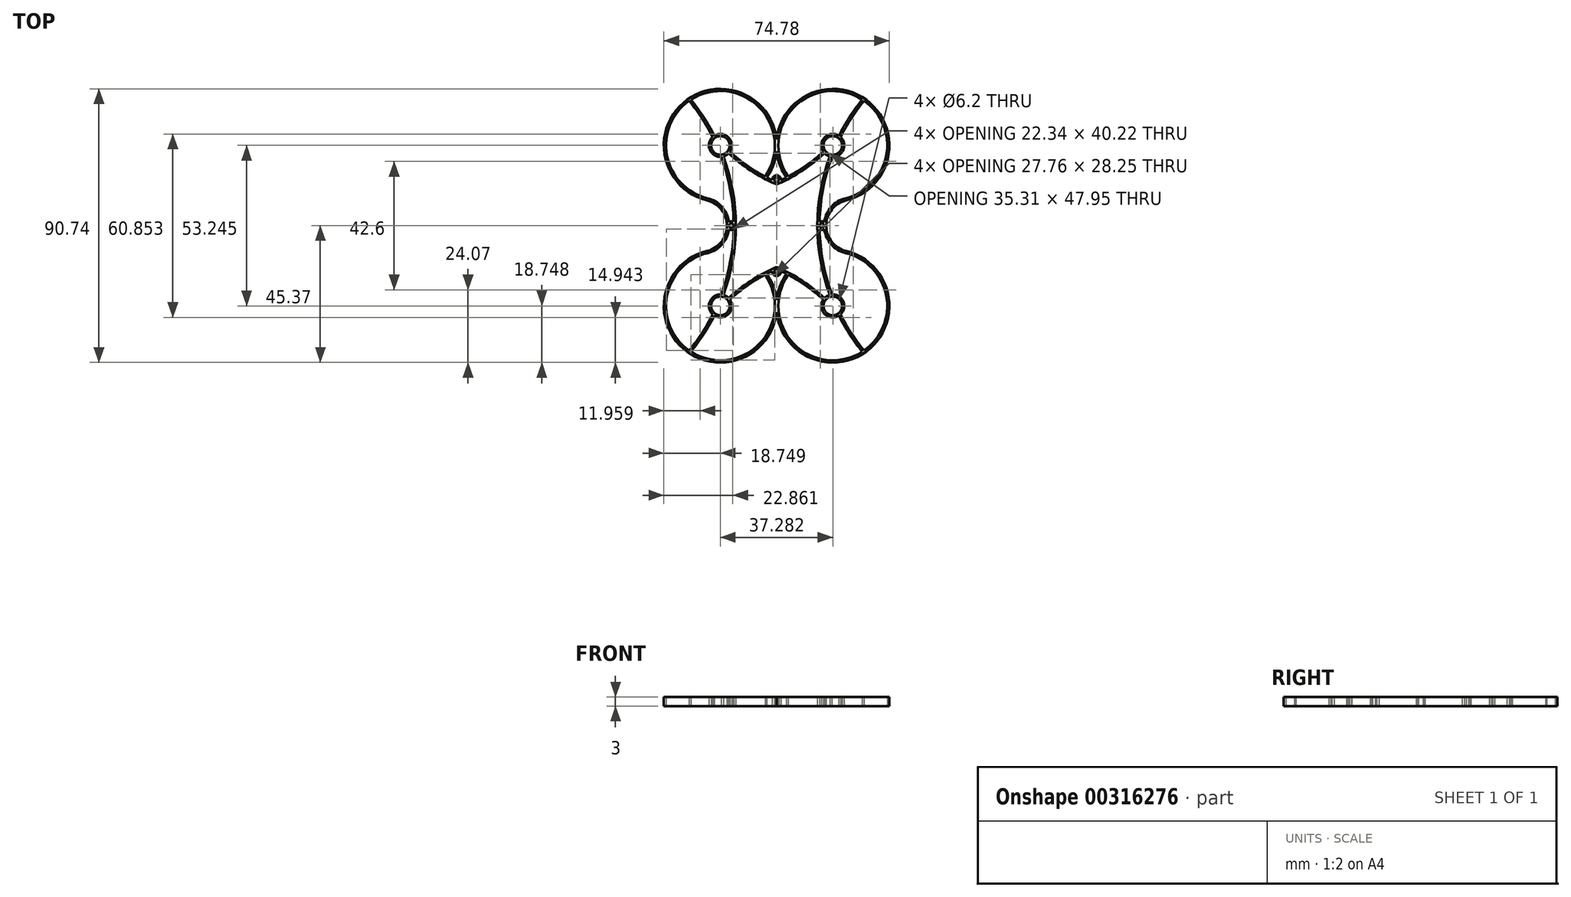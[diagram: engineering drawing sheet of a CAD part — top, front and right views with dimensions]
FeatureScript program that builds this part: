
annotation { "Feature Type Name" : "Feature", "Feature Type Description" : "" }
export const myFeature = defineFeature(function(context is Context, id is Id, definition is map)
    precondition{}
    {
        {
            var Q0;
            Q0=qCreatedBy(makeId("Top.planeOp"),FACE);
            var sketch = newSketch(context, id + "F0", { "sketchPlane" : qUnion([Q0])});
            skCircle(sketch, "E0", {"center": v(0, 0) * mm, "radius": 32.5 * mm, "construction": true});
            skLineSegment(sketch, "E1", {"start": v(0, 0) * mm, "end": v(37.3, 53.28) * mm, "construction": true});
            skPoint(sketch, "E2", {"position": v(18.64, 26.62) * mm});
            skCircle(sketch, "E3", {"center": v(18.64, 26.62) * mm, "radius": 15 * mm, "construction": true});
            skCircle(sketch, "E4", {"center": v(0, 0) * mm, "radius": 15 * mm, "construction": true});
            skPoint(sketch, "E5", {"position": v(15, 0) * mm});
            skPoint(sketch, "E6", {"position": v(0, 15.25) * mm});
            skCircle(sketch, "E7", {"center": v(0, 15.25) * mm, "radius": 0.75 * mm});
            skCircle(sketch, "E8.0", {"center": v(0, 15.25) * mm, "radius": 1.45 * mm});
            skCircle(sketch, "E9", {"center": v(15, 0) * mm, "radius": 0.75 * mm});
            skCircle(sketch, "E10.0", {"center": v(15, 0) * mm, "radius": 1.45 * mm});
            skLineSegment(sketch, "E11", {"start": v(0, 0) * mm, "end": v(0, 39.87) * mm, "construction": true});
            skCircle(sketch, "E12", {"center": v(18.64, 26.62) * mm, "radius": 18.75 * mm});
            skCircle(sketch, "E13.0", {"center": v(18.64, 26.62) * mm, "radius": 18.05 * mm});
            skArc(sketch, "E14", {"start": v(22.93, 9.09) * mm, "mid": v(17.76, 5.8) * mm, "end": v(15.75, 0) * mm});
            skArc(sketch, "E15.0", {"start": v(23.1, 8.4) * mm, "mid": v(18.31, 5.36) * mm, "end": v(16.45, 0) * mm});
            skCircle(sketch, "E16", {"center": v(18.64, 26.62) * mm, "radius": 3.1 * mm});
            skCircle(sketch, "E17.0", {"center": v(18.64, 26.62) * mm, "radius": 3.8 * mm});
            skArc(sketch, "E18", {"start": v(29, 41.4) * mm, "mid": v(28.04, 40.21) * mm, "end": v(27.12, 39) * mm});
            skArc(sketch, "E19.0", {"start": v(28.86, 42.34) * mm, "mid": v(24.21, 36.03) * mm, "end": v(20.34, 29.21) * mm});
            skArc(sketch, "E20", {"start": v(0.6, 13.93) * mm, "mid": v(8.65, 18.35) * mm, "end": v(15.91, 23.98) * mm});
            skArc(sketch, "E21.0", {"start": v(0.22, 14.53) * mm, "mid": v(8.25, 18.92) * mm, "end": v(15.47, 24.52) * mm});
            skArc(sketch, "E22.trimOffspring", {"start": v(18.64, 26.62) * mm, "mid": v(18.64, 26.63) * mm, "end": v(18.65, 26.63) * mm});
            skArc(sketch, "E23.trimOffspring", {"start": v(18.36, 22.83) * mm, "mid": v(15.29, 11.6) * mm, "end": v(14.25, 0) * mm});
            skArc(sketch, "E24.trimOffspring", {"start": v(17.66, 22.95) * mm, "mid": v(14.58, 11.66) * mm, "end": v(13.55, 0) * mm});
            skArc(sketch, "E25.trimOffspring", {"start": v(27.12, 39) * mm, "mid": v(23.77, 34.02) * mm, "end": v(20.9, 28.75) * mm});
            skSolve(sketch);
        }
        {
            var Q0;
            Q0=makeQuery(id+"F0.imprint","IMPRINT",FACE,{"disambiguationData":[TD([[makeQuery(id+"F0.imprint","IMPRINT",EDGE,{"derivedFrom":sQuery(id+"F0.wireOp",EDGE,"E7")}),-1.0]])]});
            var Q1;
            {var subQ0=sQuery(id+"F0.wireOp",EDGE,"E20");var subQ1=sQuery(id+"F0.wireOp",EDGE,"E8.0");var subQ2=makeQuery(id+"F0.imprint","INTERSECT",VERTEX,{"derivedFrom":[subQ1,subQ0]});Q1=makeQuery(id+"F0.imprint","IMPRINT",FACE,{"disambiguationData":[TD([[makeQuery(id+"F0.imprint","IMPRINT",EDGE,{"disambiguationData":[TD([[subQ2,-1.0]])],"derivedFrom":subQ1}),-1.0]])]});}
            var Q2;
            {var subQ0=sQuery(id+"F0.wireOp",EDGE,"E15.0");var subQ1=sQuery(id+"F0.wireOp",EDGE,"E10.0");var subQ2=makeQuery(id+"F0.imprint","INTERSECT",VERTEX,{"derivedFrom":[subQ1,subQ0]});Q2=makeQuery(id+"F0.imprint","IMPRINT",FACE,{"disambiguationData":[TD([[makeQuery(id+"F0.imprint","IMPRINT",EDGE,{"disambiguationData":[TD([[subQ2,-1.0]])],"derivedFrom":subQ1}),-1.0]])]});}
            var Q3;
            {var subQ0=sQuery(id+"F0.wireOp",EDGE,"E24.trimOffspring");var subQ1=sQuery(id+"F0.wireOp",EDGE,"E10.0");var subQ2=makeQuery(id+"F0.imprint","INTERSECT",VERTEX,{"derivedFrom":[subQ1,subQ0]});Q3=makeQuery(id+"F0.imprint","IMPRINT",FACE,{"disambiguationData":[TD([[makeQuery(id+"F0.imprint","IMPRINT",EDGE,{"disambiguationData":[TD([[subQ2,1.0]])],"derivedFrom":subQ1}),-1.0]])]});}
            var Q4;
            {var subQ0=sQuery(id+"F0.wireOp",EDGE,"E19.0");var subQ1=sQuery(id+"F0.wireOp",EDGE,"E12");var subQ2=makeQuery(id+"F0.imprint","INTERSECT",VERTEX,{"derivedFrom":[subQ1,subQ0]});Q4=makeQuery(id+"F0.imprint","IMPRINT",FACE,{"disambiguationData":[TD([[makeQuery(id+"F0.imprint","IMPRINT",EDGE,{"disambiguationData":[TD([[subQ2,-1.0]])],"derivedFrom":subQ1}),1.0]])]});}
            var Q5;
            {var subQ5=sQuery(id+"F0.wireOp",EDGE,"E14");var subQ7=sQuery(id+"F0.wireOp",EDGE,"E9");var subQ8=makeQuery(id+"F0.imprint","INTERSECT",VERTEX,{"derivedFrom":[subQ7,subQ5]});Q5=makeQuery(id+"F0.imprint","IMPRINT",FACE,{"disambiguationData":[TD([[makeQuery(id+"F0.imprint","IMPRINT",EDGE,{"disambiguationData":[TD([[subQ8,1.0]])],"derivedFrom":subQ7}),-1.0]])]});}
            var Q6;
            {var subQ0=sQuery(id+"F0.wireOp",EDGE,"E21.0");var subQ1=sQuery(id+"F0.wireOp",EDGE,"E12");var subQ2=makeQuery(id+"F0.imprint","INTERSECT",VERTEX,{"derivedFrom":[subQ1,subQ0]});Q6=makeQuery(id+"F0.imprint","IMPRINT",FACE,{"disambiguationData":[TD([[makeQuery(id+"F0.imprint","IMPRINT",EDGE,{"disambiguationData":[TD([[subQ2,-1.0]])],"derivedFrom":subQ1}),1.0]])]});}
            var Q7;
            {var subQ0=sQuery(id+"F0.wireOp",EDGE,"E24.trimOffspring");var subQ1=sQuery(id+"F0.wireOp",EDGE,"E12");var subQ2=makeQuery(id+"F0.imprint","INTERSECT",VERTEX,{"derivedFrom":[subQ1,subQ0]});Q7=makeQuery(id+"F0.imprint","IMPRINT",FACE,{"disambiguationData":[TD([[makeQuery(id+"F0.imprint","IMPRINT",EDGE,{"disambiguationData":[TD([[subQ2,-1.0]])],"derivedFrom":subQ1}),1.0]])]});}
            var Q8;
            {var subQ6=sQuery(id+"F0.wireOp",EDGE,"E12");var subQ8=makeQuery(id+"F0.imprint","INTERSECT",VERTEX,{"derivedFrom":[subQ6,sQuery(id+"F0.wireOp",EDGE,"E15.0")]});Q8=makeQuery(id+"F0.imprint","IMPRINT",FACE,{"disambiguationData":[TD([[makeQuery(id+"F0.imprint","IMPRINT",EDGE,{"disambiguationData":[TD([[subQ8,1.0]])],"derivedFrom":subQ6}),1.0]])]});}
            var Q9;
            {var subQ0=sQuery(id+"F0.wireOp",EDGE,"E14");var subQ1=sQuery(id+"F0.wireOp",EDGE,"E9");var subQ2=makeQuery(id+"F0.imprint","INTERSECT",VERTEX,{"derivedFrom":[subQ1,subQ0]});Q9=makeQuery(id+"F0.imprint","IMPRINT",FACE,{"disambiguationData":[TD([[makeQuery(id+"F0.imprint","IMPRINT",EDGE,{"disambiguationData":[TD([[subQ2,-1.0]])],"derivedFrom":subQ1}),-1.0]])]});}
            var Q10;
            {var subQ0=sQuery(id+"F0.wireOp",EDGE,"E24.trimOffspring");var subQ1=sQuery(id+"F0.wireOp",EDGE,"E13.0");var subQ2=makeQuery(id+"F0.imprint","INTERSECT",VERTEX,{"derivedFrom":[subQ1,subQ0]});Q10=makeQuery(id+"F0.imprint","IMPRINT",FACE,{"disambiguationData":[TD([[makeQuery(id+"F0.imprint","IMPRINT",EDGE,{"disambiguationData":[TD([[subQ2,-1.0]])],"derivedFrom":subQ1}),1.0]])]});}
            var Q11;
            {var subQ0=sQuery(id+"F0.wireOp",EDGE,"E21.0");var subQ1=sQuery(id+"F0.wireOp",EDGE,"E13.0");var subQ2=makeQuery(id+"F0.imprint","INTERSECT",VERTEX,{"derivedFrom":[subQ1,subQ0]});Q11=makeQuery(id+"F0.imprint","IMPRINT",FACE,{"disambiguationData":[TD([[makeQuery(id+"F0.imprint","IMPRINT",EDGE,{"disambiguationData":[TD([[subQ2,-1.0]])],"derivedFrom":subQ1}),1.0]])]});}
            var Q12;
            {var subQ5=sQuery(id+"F0.wireOp",EDGE,"E16");var subQ8=sQuery(id+"F0.wireOp",EDGE,"E19.0");var subQ10=makeQuery(id+"F0.imprint","INTERSECT",VERTEX,{"derivedFrom":[subQ5,subQ8]});Q12=makeQuery(id+"F0.imprint","IMPRINT",FACE,{"disambiguationData":[TD([[makeQuery(id+"F0.imprint","IMPRINT",EDGE,{"disambiguationData":[TD([[subQ10,-1.0]])],"derivedFrom":subQ5}),-1.0]])]});}
            var Q13;
            {var subQ0=sQuery(id+"F0.wireOp",EDGE,"E19.0");var subQ1=sQuery(id+"F0.wireOp",EDGE,"E16");var subQ2=makeQuery(id+"F0.imprint","INTERSECT",VERTEX,{"derivedFrom":[subQ1,subQ0]});Q13=makeQuery(id+"F0.imprint","IMPRINT",FACE,{"disambiguationData":[TD([[makeQuery(id+"F0.imprint","IMPRINT",EDGE,{"disambiguationData":[TD([[subQ2,1.0]])],"derivedFrom":subQ1}),-1.0]])]});}
            var Q14;
            {var subQ5=sQuery(id+"F0.wireOp",EDGE,"E18");Q14=makeQuery(id+"F0.imprint","IMPRINT",FACE,{"disambiguationData":[TD([[makeQuery(id+"F0.imprint","IMPRINT",EDGE,{"derivedFrom":subQ5}),-1.0]])]});}
            extrude(context, id + "F1", {"entities" : qUnion([Q0, Q1, Q2, Q3, Q4, Q5, Q6, Q7, Q8, Q9, Q10, Q11, Q12, Q13, Q14]), "depth" : 3 * mm});
        }
        {
            var Q0;
            Q0=makeQuery(id+"F1.opExtrude","SWEPT_BODY",BODY,{"disambiguationData":[OSD([sQuery(id+"F0.wireOp",EDGE,"E7"),sQuery(id+"F0.wireOp",EDGE,"E8.0"),sQuery(id+"F0.wireOp",EDGE,"E9"),sQuery(id+"F0.wireOp",EDGE,"E10.0"),sQuery(id+"F0.wireOp",EDGE,"E12"),sQuery(id+"F0.wireOp",EDGE,"E13.0"),sQuery(id+"F0.wireOp",EDGE,"E14"),sQuery(id+"F0.wireOp",EDGE,"E15.0"),sQuery(id+"F0.wireOp",EDGE,"E16"),sQuery(id+"F0.wireOp",EDGE,"E17.0"),sQuery(id+"F0.wireOp",EDGE,"E18"),sQuery(id+"F0.wireOp",EDGE,"E19.0"),sQuery(id+"F0.wireOp",EDGE,"E20"),sQuery(id+"F0.wireOp",EDGE,"E21.0"),sQuery(id+"F0.wireOp",EDGE,"E23.trimOffspring"),sQuery(id+"F0.wireOp",EDGE,"E24.trimOffspring"),sQuery(id+"F0.wireOp",EDGE,"E25.trimOffspring")])]});
            var Q1;
            Q1=qCreatedBy(makeId("Front.planeOp"),FACE);
            mirror(context, id + "F2", {"operationType" : NewBodyOperationType.ADD, "entities" : qUnion([Q0]), "mirrorPlane" : qUnion([Q1])});
        }
        {
            var Q0;
            Q0=makeQuery(id+"F1.opExtrude","SWEPT_BODY",BODY,{"disambiguationData":[OSD([sQuery(id+"F0.wireOp",EDGE,"E7"),sQuery(id+"F0.wireOp",EDGE,"E8.0"),sQuery(id+"F0.wireOp",EDGE,"E9"),sQuery(id+"F0.wireOp",EDGE,"E10.0"),sQuery(id+"F0.wireOp",EDGE,"E12"),sQuery(id+"F0.wireOp",EDGE,"E13.0"),sQuery(id+"F0.wireOp",EDGE,"E14"),sQuery(id+"F0.wireOp",EDGE,"E15.0"),sQuery(id+"F0.wireOp",EDGE,"E16"),sQuery(id+"F0.wireOp",EDGE,"E17.0"),sQuery(id+"F0.wireOp",EDGE,"E18"),sQuery(id+"F0.wireOp",EDGE,"E19.0"),sQuery(id+"F0.wireOp",EDGE,"E20"),sQuery(id+"F0.wireOp",EDGE,"E21.0"),sQuery(id+"F0.wireOp",EDGE,"E23.trimOffspring"),sQuery(id+"F0.wireOp",EDGE,"E24.trimOffspring"),sQuery(id+"F0.wireOp",EDGE,"E25.trimOffspring")])]});
            var Q1;
            Q1=qCreatedBy(makeId("Right.planeOp"),FACE);
            mirror(context, id + "F3", {"operationType" : NewBodyOperationType.ADD, "entities" : qUnion([Q0]), "mirrorPlane" : qUnion([Q1])});
        }
    });
